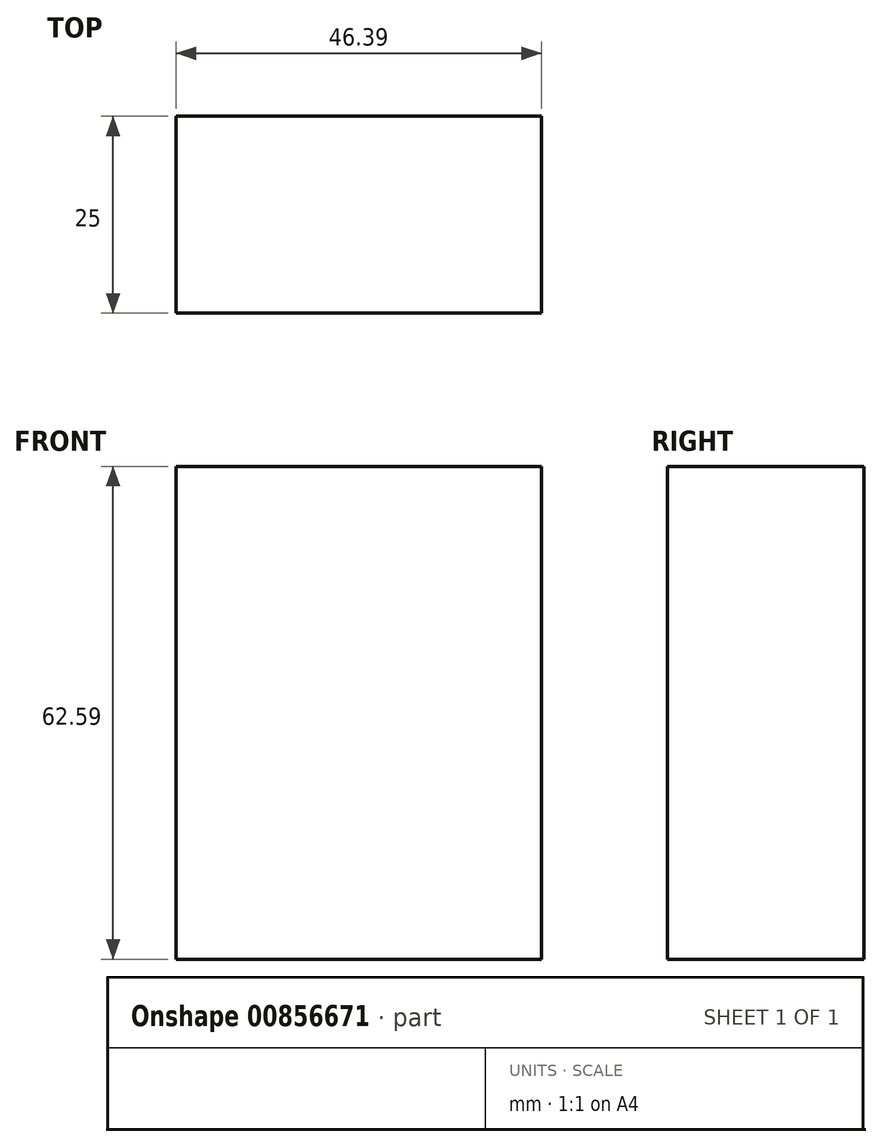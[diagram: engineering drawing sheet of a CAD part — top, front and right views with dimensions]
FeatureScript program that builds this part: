
annotation { "Feature Type Name" : "Feature", "Feature Type Description" : "" }
export const myFeature = defineFeature(function(context is Context, id is Id, definition is map)
    precondition{}
    {
        {
            var Q0;
            Q0=qCreatedBy(makeId("Front.planeOp"),FACE);
            var sketch = newSketch(context, id + "F0", { "sketchPlane" : qUnion([Q0])});
            skLineSegment(sketch, "E0.bottom", {"start": v(-166.24, 22.78) * mm, "end": v(-119.85, 22.78) * mm});
            skLineSegment(sketch, "E0.top", {"start": v(-166.24, -39.8) * mm, "end": v(-119.85, -39.8) * mm});
            skLineSegment(sketch, "E0.left", {"start": v(-166.24, 22.78) * mm, "end": v(-166.24, -39.8) * mm});
            skLineSegment(sketch, "E0.right", {"start": v(-119.85, 22.78) * mm, "end": v(-119.85, -39.8) * mm});
            skSolve(sketch);
        }
        {
            var Q0;
            Q0 = qSketchRegion(id + "F0", true);
            extrude(context, id + "F1", {"entities" : qUnion([Q0]), "depth" : 25 * mm, "offsetDistance" : 25 * mm});
        }
        {
            var Q0;
            Q0=makeQuery(id+"F1.opExtrude","SWEPT_BODY",BODY,{"disambiguationData":[OSD([sQuery(id+"F0.wireOp",EDGE,"E0.bottom"),sQuery(id+"F0.wireOp",EDGE,"E0.top"),sQuery(id+"F0.wireOp",EDGE,"E0.left"),sQuery(id+"F0.wireOp",EDGE,"E0.right")])]});
            var Q1;
            Q1=makeQuery(id+"F1.opExtrude","CAP_EDGE",EDGE,{"disambiguationData":[OSD([sQuery(id+"F0.wireOp",EDGE,"E0.bottom")])],"isStart":false});
            circularPattern(context, id + "F2", {"entities" : qUnion([Q0]), "axis" : qUnion([Q1]), "angle" : 360 * degree, "instanceCount" : 10});
        }
    });
